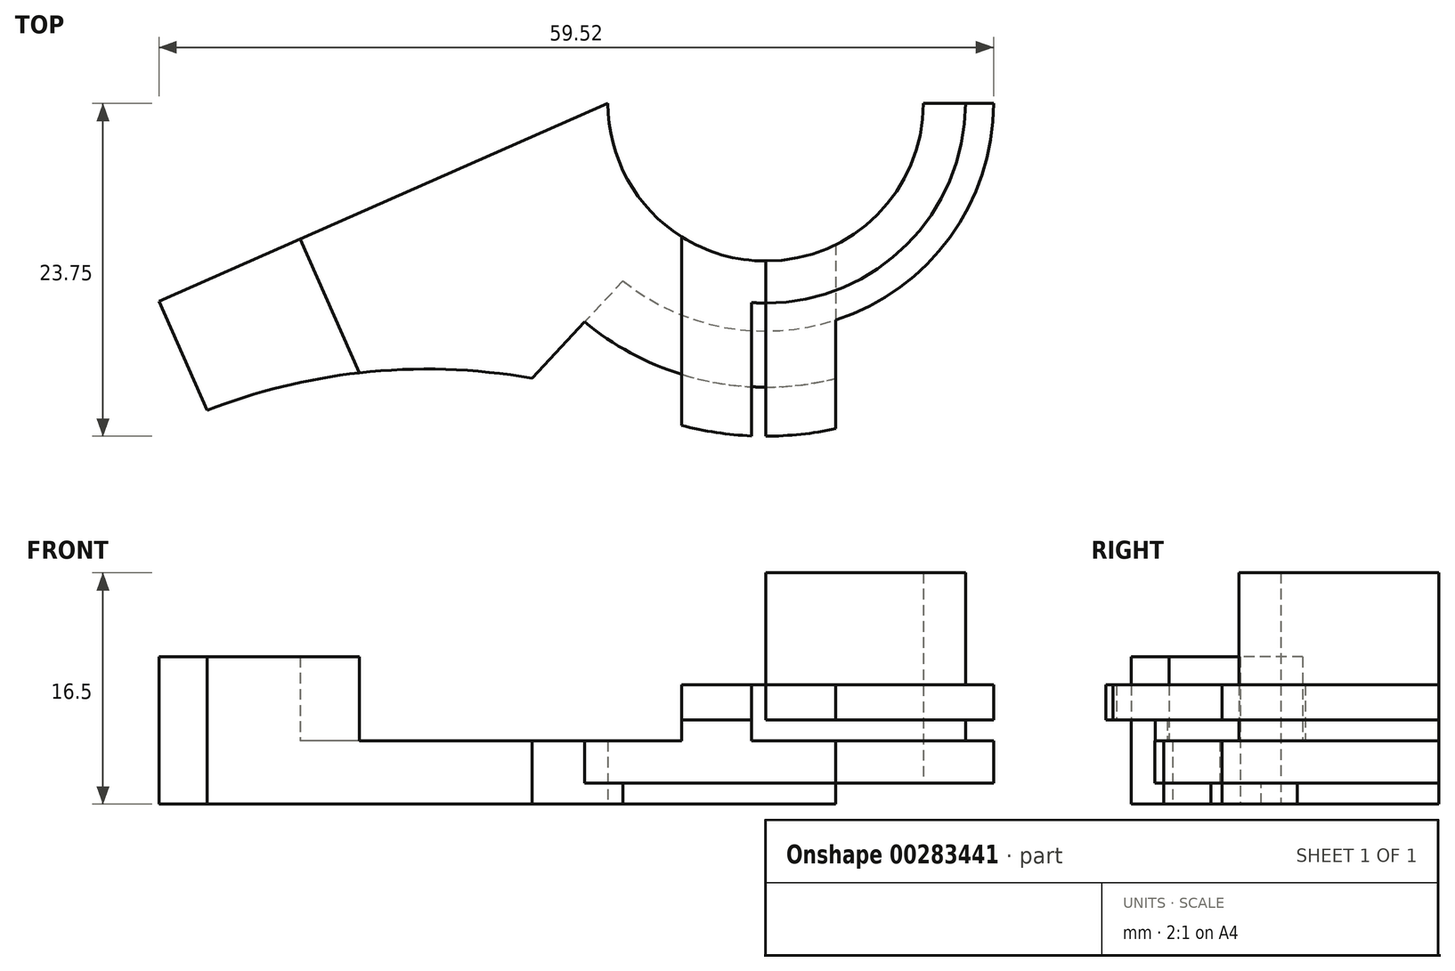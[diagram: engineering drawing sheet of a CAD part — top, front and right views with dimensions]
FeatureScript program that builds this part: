
annotation { "Feature Type Name" : "Feature", "Feature Type Description" : "" }
export const myFeature = defineFeature(function(context is Context, id is Id, definition is map)
    precondition{}
    {
        {
            var Q0;
            Q0=qCreatedBy(makeId("Top.planeOp"),FACE);
            var sketch = newSketch(context, id + "F0", { "sketchPlane" : qUnion([Q0])});
            skCircle(sketch, "E0", {"center": v(0, 0) * mm, "radius": 11.25 * mm});
            skCircle(sketch, "E1.0", {"center": v(0, 0) * mm, "radius": 14.25 * mm});
            skCircle(sketch, "E2.0", {"center": v(0, 0) * mm, "radius": 16.25 * mm});
            skCircle(sketch, "E3.0", {"center": v(0, 0) * mm, "radius": 20.25 * mm});
            skLineSegment(sketch, "E4", {"start": v(-11.25, 0) * mm, "end": v(-43.27, -14.14) * mm});
            skLineSegment(sketch, "E5", {"start": v(-43.27, -14.14) * mm, "end": v(-39.83, -21.91) * mm});
            skLineSegment(sketch, "E6", {"start": v(-12.91, -15.6) * mm, "end": v(-16.67, -19.62) * mm});
            skArc(sketch, "E7", {"start": v(-16.67, -19.62) * mm, "mid": v(-28.4, -19.17) * mm, "end": v(-39.83, -21.91) * mm});
            skLineSegment(sketch, "E8", {"start": v(-12.91, -15.6) * mm, "end": v(-10.18, -12.67) * mm});
            skLineSegment(sketch, "E9", {"start": v(-33.2, -9.7) * mm, "end": v(-29, -19.23) * mm});
            skLineSegment(sketch, "E10", {"start": v(0, 0) * mm, "end": v(0, -47.45) * mm});
            skCircle(sketch, "E11.0", {"center": v(0, 0) * mm, "radius": 23.75 * mm});
            skLineSegment(sketch, "E12.0", {"start": v(-6, 0) * mm, "end": v(-6, -47.45) * mm});
            skLineSegment(sketch, "E13.0", {"start": v(5, 0) * mm, "end": v(5, -47.45) * mm});
            skLineSegment(sketch, "E14", {"start": v(0, 0) * mm, "end": v(33.67, 0) * mm});
            skCircle(sketch, "E15.0", {"center": v(0, 0) * mm, "radius": 15.25 * mm});
            skLineSegment(sketch, "E16", {"start": v(-10.18, -12.67) * mm, "end": v(-9.5, -11.94) * mm});
            skLineSegment(sketch, "E17", {"start": v(-1, -47.36) * mm, "end": v(-1, 0) * mm});
            skSolve(sketch);
        }
        {
            var Q0;
            {var subQ0=sQuery(id+"F0.wireOp",EDGE,"E5");Q0=makeQuery(id+"F0.imprint","IMPRINT",FACE,{"disambiguationData":[TD([[makeQuery(id+"F0.imprint","IMPRINT",EDGE,{"derivedFrom":subQ0}),1.0]])]});}
            var Q1;
            {var subQ0=sQuery(id+"F0.wireOp",EDGE,"E9");Q1=makeQuery(id+"F0.imprint","IMPRINT",FACE,{"disambiguationData":[TD([[makeQuery(id+"F0.imprint","IMPRINT",EDGE,{"derivedFrom":subQ0}),1.0]])]});}
            var Q2;
            {var subQ3=sQuery(id+"F0.wireOp",EDGE,"E4");var subQ5=sQuery(id+"F0.wireOp",EDGE,"E11.0");var subQ6=makeQuery(id+"F0.imprint","INTERSECT",VERTEX,{"derivedFrom":[subQ3,subQ5]});Q2=makeQuery(id+"F0.imprint","IMPRINT",FACE,{"disambiguationData":[TD([[makeQuery(id+"F0.imprint","IMPRINT",EDGE,{"disambiguationData":[TD([[subQ6,1.0]])],"derivedFrom":subQ3}),1.0]])]});}
            var Q3;
            {var subQ0=sQuery(id+"F0.wireOp",EDGE,"E8");Q3=makeQuery(id+"F0.imprint","IMPRINT",FACE,{"disambiguationData":[TD([[makeQuery(id+"F0.imprint","IMPRINT",EDGE,{"derivedFrom":subQ0}),1.0]])]});}
            var Q4;
            {var subQ0=sQuery(id+"F0.wireOp",EDGE,"E16");Q4=makeQuery(id+"F0.imprint","IMPRINT",FACE,{"disambiguationData":[TD([[makeQuery(id+"F0.imprint","IMPRINT",EDGE,{"derivedFrom":subQ0}),1.0]])]});}
            var Q5;
            {var subQ0=sQuery(id+"F0.wireOp",EDGE,"E16");Q5=makeQuery(id+"F0.imprint","IMPRINT",FACE,{"disambiguationData":[TD([[makeQuery(id+"F0.imprint","IMPRINT",EDGE,{"derivedFrom":subQ0}),-1.0]])]});}
            var Q6;
            {var subQ0=sQuery(id+"F0.wireOp",EDGE,"E12.0");var subQ1=sQuery(id+"F0.wireOp",EDGE,"E2.0");var subQ2=makeQuery(id+"F0.imprint","INTERSECT",VERTEX,{"derivedFrom":[subQ1,subQ0]});Q6=makeQuery(id+"F0.imprint","IMPRINT",FACE,{"disambiguationData":[TD([[makeQuery(id+"F0.imprint","IMPRINT",EDGE,{"disambiguationData":[TD([[subQ2,-1.0]])],"derivedFrom":subQ1}),1.0]])]});}
            var Q7;
            {var subQ0=sQuery(id+"F0.wireOp",EDGE,"E10");var subQ1=sQuery(id+"F0.wireOp",EDGE,"E2.0");var subQ2=makeQuery(id+"F0.imprint","INTERSECT",VERTEX,{"derivedFrom":[subQ1,subQ0]});Q7=makeQuery(id+"F0.imprint","IMPRINT",FACE,{"disambiguationData":[TD([[makeQuery(id+"F0.imprint","IMPRINT",EDGE,{"disambiguationData":[TD([[subQ2,-1.0]])],"derivedFrom":subQ1}),1.0]])]});}
            var Q8;
            {var subQ0=sQuery(id+"F0.wireOp",EDGE,"E8");Q8=makeQuery(id+"F0.imprint","IMPRINT",FACE,{"disambiguationData":[TD([[makeQuery(id+"F0.imprint","IMPRINT",EDGE,{"derivedFrom":subQ0}),-1.0]])]});}
            var Q9;
            {var subQ0=sQuery(id+"F0.wireOp",EDGE,"E12.0");var subQ1=sQuery(id+"F0.wireOp",EDGE,"E2.0");var subQ2=makeQuery(id+"F0.imprint","INTERSECT",VERTEX,{"derivedFrom":[subQ1,subQ0]});Q9=makeQuery(id+"F0.imprint","IMPRINT",FACE,{"disambiguationData":[TD([[makeQuery(id+"F0.imprint","IMPRINT",EDGE,{"disambiguationData":[TD([[subQ2,-1.0]])],"derivedFrom":subQ1}),-1.0]])]});}
            var Q10;
            {var subQ0=sQuery(id+"F0.wireOp",EDGE,"E10");var subQ1=sQuery(id+"F0.wireOp",EDGE,"E2.0");var subQ2=makeQuery(id+"F0.imprint","INTERSECT",VERTEX,{"derivedFrom":[subQ1,subQ0]});Q10=makeQuery(id+"F0.imprint","IMPRINT",FACE,{"disambiguationData":[TD([[makeQuery(id+"F0.imprint","IMPRINT",EDGE,{"disambiguationData":[TD([[subQ2,-1.0]])],"derivedFrom":subQ1}),-1.0]])]});}
            var Q11;
            {var subQ0=sQuery(id+"F0.wireOp",EDGE,"E4");var subQ1=sQuery(id+"F0.wireOp",EDGE,"E0");var subQ2=makeQuery(id+"F0.imprint","INTERSECT",VERTEX,{"derivedFrom":[subQ1,subQ0]});Q11=makeQuery(id+"F0.imprint","IMPRINT",FACE,{"disambiguationData":[TD([[makeQuery(id+"F0.imprint","IMPRINT",EDGE,{"disambiguationData":[TD([[subQ2,-1.0]])],"derivedFrom":subQ1}),-1.0]])]});}
            var Q12;
            {var subQ0=sQuery(id+"F0.wireOp",EDGE,"E4");var subQ1=sQuery(id+"F0.wireOp",EDGE,"E1.0");var subQ2=makeQuery(id+"F0.imprint","INTERSECT",VERTEX,{"derivedFrom":[subQ1,subQ0]});Q12=makeQuery(id+"F0.imprint","IMPRINT",FACE,{"disambiguationData":[TD([[makeQuery(id+"F0.imprint","IMPRINT",EDGE,{"disambiguationData":[TD([[subQ2,-1.0]])],"derivedFrom":subQ1}),-1.0]])]});}
            var Q13;
            {var subQ0=sQuery(id+"F0.wireOp",EDGE,"E12.0");var subQ1=sQuery(id+"F0.wireOp",EDGE,"E0");var subQ2=makeQuery(id+"F0.imprint","INTERSECT",VERTEX,{"derivedFrom":[subQ1,subQ0]});Q13=makeQuery(id+"F0.imprint","IMPRINT",FACE,{"disambiguationData":[TD([[makeQuery(id+"F0.imprint","IMPRINT",EDGE,{"disambiguationData":[TD([[subQ2,-1.0]])],"derivedFrom":subQ1}),-1.0]])]});}
            var Q14;
            {var subQ0=sQuery(id+"F0.wireOp",EDGE,"E12.0");var subQ1=sQuery(id+"F0.wireOp",EDGE,"E1.0");var subQ2=makeQuery(id+"F0.imprint","INTERSECT",VERTEX,{"derivedFrom":[subQ1,subQ0]});Q14=makeQuery(id+"F0.imprint","IMPRINT",FACE,{"disambiguationData":[TD([[makeQuery(id+"F0.imprint","IMPRINT",EDGE,{"disambiguationData":[TD([[subQ2,-1.0]])],"derivedFrom":subQ1}),-1.0]])]});}
            var Q15;
            {var subQ0=sQuery(id+"F0.wireOp",EDGE,"E10");var subQ1=sQuery(id+"F0.wireOp",EDGE,"E0");var subQ2=makeQuery(id+"F0.imprint","INTERSECT",VERTEX,{"derivedFrom":[subQ1,subQ0]});Q15=makeQuery(id+"F0.imprint","IMPRINT",FACE,{"disambiguationData":[TD([[makeQuery(id+"F0.imprint","IMPRINT",EDGE,{"disambiguationData":[TD([[subQ2,-1.0]])],"derivedFrom":subQ1}),-1.0]])]});}
            var Q16;
            {var subQ0=sQuery(id+"F0.wireOp",EDGE,"E10");var subQ1=sQuery(id+"F0.wireOp",EDGE,"E1.0");var subQ2=makeQuery(id+"F0.imprint","INTERSECT",VERTEX,{"derivedFrom":[subQ1,subQ0]});Q16=makeQuery(id+"F0.imprint","IMPRINT",FACE,{"disambiguationData":[TD([[makeQuery(id+"F0.imprint","IMPRINT",EDGE,{"disambiguationData":[TD([[subQ2,-1.0]])],"derivedFrom":subQ1}),-1.0]])]});}
            var Q17;
            {var subQ0=sQuery(id+"F0.wireOp",EDGE,"E14");var subQ1=sQuery(id+"F0.wireOp",EDGE,"E0");var subQ2=makeQuery(id+"F0.imprint","INTERSECT",VERTEX,{"derivedFrom":[subQ1,subQ0]});Q17=makeQuery(id+"F0.imprint","IMPRINT",FACE,{"disambiguationData":[TD([[makeQuery(id+"F0.imprint","IMPRINT",EDGE,{"disambiguationData":[TD([[subQ2,1.0]])],"derivedFrom":subQ1}),-1.0]])]});}
            var Q18;
            {var subQ0=sQuery(id+"F0.wireOp",EDGE,"E14");var subQ1=sQuery(id+"F0.wireOp",EDGE,"E1.0");var subQ2=makeQuery(id+"F0.imprint","INTERSECT",VERTEX,{"derivedFrom":[subQ1,subQ0]});Q18=makeQuery(id+"F0.imprint","IMPRINT",FACE,{"disambiguationData":[TD([[makeQuery(id+"F0.imprint","IMPRINT",EDGE,{"disambiguationData":[TD([[subQ2,1.0]])],"derivedFrom":subQ1}),-1.0]])]});}
            var Q19;
            {var subQ0=sQuery(id+"F0.wireOp",EDGE,"E14");var subQ1=sQuery(id+"F0.wireOp",EDGE,"E2.0");var subQ2=makeQuery(id+"F0.imprint","INTERSECT",VERTEX,{"derivedFrom":[subQ1,subQ0]});Q19=makeQuery(id+"F0.imprint","IMPRINT",FACE,{"disambiguationData":[TD([[makeQuery(id+"F0.imprint","IMPRINT",EDGE,{"disambiguationData":[TD([[subQ2,1.0]])],"derivedFrom":subQ1}),1.0]])]});}
            var Q20;
            {var subQ0=sQuery(id+"F0.wireOp",EDGE,"E17");var subQ1=sQuery(id+"F0.wireOp",EDGE,"E2.0");var subQ2=makeQuery(id+"F0.imprint","INTERSECT",VERTEX,{"derivedFrom":[subQ1,subQ0]});Q20=makeQuery(id+"F0.imprint","IMPRINT",FACE,{"disambiguationData":[TD([[makeQuery(id+"F0.imprint","IMPRINT",EDGE,{"disambiguationData":[TD([[subQ2,-1.0]])],"derivedFrom":subQ1}),-1.0]])]});}
            var Q21;
            {var subQ0=sQuery(id+"F0.wireOp",EDGE,"E17");var subQ1=sQuery(id+"F0.wireOp",EDGE,"E2.0");var subQ2=makeQuery(id+"F0.imprint","INTERSECT",VERTEX,{"derivedFrom":[subQ1,subQ0]});Q21=makeQuery(id+"F0.imprint","IMPRINT",FACE,{"disambiguationData":[TD([[makeQuery(id+"F0.imprint","IMPRINT",EDGE,{"disambiguationData":[TD([[subQ2,-1.0]])],"derivedFrom":subQ1}),1.0]])]});}
            var Q22;
            {var subQ0=sQuery(id+"F0.wireOp",EDGE,"E17");var subQ1=sQuery(id+"F0.wireOp",EDGE,"E1.0");var subQ2=makeQuery(id+"F0.imprint","INTERSECT",VERTEX,{"derivedFrom":[subQ1,subQ0]});Q22=makeQuery(id+"F0.imprint","IMPRINT",FACE,{"disambiguationData":[TD([[makeQuery(id+"F0.imprint","IMPRINT",EDGE,{"disambiguationData":[TD([[subQ2,-1.0]])],"derivedFrom":subQ1}),-1.0]])]});}
            var Q23;
            {var subQ0=sQuery(id+"F0.wireOp",EDGE,"E17");var subQ1=sQuery(id+"F0.wireOp",EDGE,"E0");var subQ2=makeQuery(id+"F0.imprint","INTERSECT",VERTEX,{"derivedFrom":[subQ1,subQ0]});Q23=makeQuery(id+"F0.imprint","IMPRINT",FACE,{"disambiguationData":[TD([[makeQuery(id+"F0.imprint","IMPRINT",EDGE,{"disambiguationData":[TD([[subQ2,-1.0]])],"derivedFrom":subQ1}),-1.0]])]});}
            extrude(context, id + "F1", {"entities" : qUnion([Q0, Q1, Q2, Q3, Q4, Q5, Q6, Q7, Q8, Q9, Q10, Q11, Q12, Q13, Q14, Q15, Q16, Q17, Q18, Q19, Q20, Q21, Q22, Q23]), "depth" : 3 * mm});
        }
        {
            var Q0;
            {var subQ0=sQuery(id+"F0.wireOp",EDGE,"E14");var subQ1=sQuery(id+"F0.wireOp",EDGE,"E0");var subQ2=makeQuery(id+"F0.imprint","INTERSECT",VERTEX,{"derivedFrom":[subQ1,subQ0]});Q0=makeQuery(id+"F0.imprint","IMPRINT",FACE,{"disambiguationData":[TD([[makeQuery(id+"F0.imprint","IMPRINT",EDGE,{"disambiguationData":[TD([[subQ2,1.0]])],"derivedFrom":subQ1}),-1.0]])]});}
            var Q1;
            {var subQ0=sQuery(id+"F0.wireOp",EDGE,"E10");var subQ1=sQuery(id+"F0.wireOp",EDGE,"E0");var subQ2=makeQuery(id+"F0.imprint","INTERSECT",VERTEX,{"derivedFrom":[subQ1,subQ0]});Q1=makeQuery(id+"F0.imprint","IMPRINT",FACE,{"disambiguationData":[TD([[makeQuery(id+"F0.imprint","IMPRINT",EDGE,{"disambiguationData":[TD([[subQ2,-1.0]])],"derivedFrom":subQ1}),-1.0]])]});}
            var Q2;
            {var subQ0=sQuery(id+"F0.wireOp",EDGE,"E17");var subQ1=sQuery(id+"F0.wireOp",EDGE,"E0");var subQ2=makeQuery(id+"F0.imprint","INTERSECT",VERTEX,{"derivedFrom":[subQ1,subQ0]});Q2=makeQuery(id+"F0.imprint","IMPRINT",FACE,{"disambiguationData":[TD([[makeQuery(id+"F0.imprint","IMPRINT",EDGE,{"disambiguationData":[TD([[subQ2,-1.0]])],"derivedFrom":subQ1}),-1.0]])]});}
            var Q3;
            {var subQ0=sQuery(id+"F0.wireOp",EDGE,"E12.0");var subQ1=sQuery(id+"F0.wireOp",EDGE,"E0");var subQ2=makeQuery(id+"F0.imprint","INTERSECT",VERTEX,{"derivedFrom":[subQ1,subQ0]});Q3=makeQuery(id+"F0.imprint","IMPRINT",FACE,{"disambiguationData":[TD([[makeQuery(id+"F0.imprint","IMPRINT",EDGE,{"disambiguationData":[TD([[subQ2,-1.0]])],"derivedFrom":subQ1}),-1.0]])]});}
            var Q4;
            {var subQ0=sQuery(id+"F0.wireOp",EDGE,"E12.0");var subQ1=sQuery(id+"F0.wireOp",EDGE,"E1.0");var subQ2=makeQuery(id+"F0.imprint","INTERSECT",VERTEX,{"derivedFrom":[subQ1,subQ0]});Q4=makeQuery(id+"F0.imprint","IMPRINT",FACE,{"disambiguationData":[TD([[makeQuery(id+"F0.imprint","IMPRINT",EDGE,{"disambiguationData":[TD([[subQ2,-1.0]])],"derivedFrom":subQ1}),-1.0]])]});}
            var Q5;
            {var subQ0=sQuery(id+"F0.wireOp",EDGE,"E12.0");var subQ1=sQuery(id+"F0.wireOp",EDGE,"E2.0");var subQ2=makeQuery(id+"F0.imprint","INTERSECT",VERTEX,{"derivedFrom":[subQ1,subQ0]});Q5=makeQuery(id+"F0.imprint","IMPRINT",FACE,{"disambiguationData":[TD([[makeQuery(id+"F0.imprint","IMPRINT",EDGE,{"disambiguationData":[TD([[subQ2,-1.0]])],"derivedFrom":subQ1}),1.0]])]});}
            var Q6;
            {var subQ0=sQuery(id+"F0.wireOp",EDGE,"E12.0");var subQ1=sQuery(id+"F0.wireOp",EDGE,"E2.0");var subQ2=makeQuery(id+"F0.imprint","INTERSECT",VERTEX,{"derivedFrom":[subQ1,subQ0]});Q6=makeQuery(id+"F0.imprint","IMPRINT",FACE,{"disambiguationData":[TD([[makeQuery(id+"F0.imprint","IMPRINT",EDGE,{"disambiguationData":[TD([[subQ2,-1.0]])],"derivedFrom":subQ1}),-1.0]])]});}
            extrude(context, id + "F2", {"entities" : qUnion([Q0, Q1, Q2, Q3, Q4, Q5, Q6]), "operationType" : NewBodyOperationType.ADD, "depth" : 4.5 * mm});
        }
        {
            var Q0;
            {var subQ0=sQuery(id+"F0.wireOp",EDGE,"E14");var subQ1=sQuery(id+"F0.wireOp",EDGE,"E0");var subQ2=makeQuery(id+"F0.imprint","INTERSECT",VERTEX,{"derivedFrom":[subQ1,subQ0]});Q0=makeQuery(id+"F0.imprint","IMPRINT",FACE,{"disambiguationData":[TD([[makeQuery(id+"F0.imprint","IMPRINT",EDGE,{"disambiguationData":[TD([[subQ2,1.0]])],"derivedFrom":subQ1}),-1.0]])]});}
            var Q1;
            {var subQ0=sQuery(id+"F0.wireOp",EDGE,"E14");var subQ1=sQuery(id+"F0.wireOp",EDGE,"E1.0");var subQ2=makeQuery(id+"F0.imprint","INTERSECT",VERTEX,{"derivedFrom":[subQ1,subQ0]});Q1=makeQuery(id+"F0.imprint","IMPRINT",FACE,{"disambiguationData":[TD([[makeQuery(id+"F0.imprint","IMPRINT",EDGE,{"disambiguationData":[TD([[subQ2,1.0]])],"derivedFrom":subQ1}),-1.0]])]});}
            var Q2;
            {var subQ0=sQuery(id+"F0.wireOp",EDGE,"E14");var subQ1=sQuery(id+"F0.wireOp",EDGE,"E2.0");var subQ2=makeQuery(id+"F0.imprint","INTERSECT",VERTEX,{"derivedFrom":[subQ1,subQ0]});Q2=makeQuery(id+"F0.imprint","IMPRINT",FACE,{"disambiguationData":[TD([[makeQuery(id+"F0.imprint","IMPRINT",EDGE,{"disambiguationData":[TD([[subQ2,1.0]])],"derivedFrom":subQ1}),1.0]])]});}
            var Q3;
            {var subQ0=sQuery(id+"F0.wireOp",EDGE,"E10");var subQ1=sQuery(id+"F0.wireOp",EDGE,"E0");var subQ2=makeQuery(id+"F0.imprint","INTERSECT",VERTEX,{"derivedFrom":[subQ1,subQ0]});Q3=makeQuery(id+"F0.imprint","IMPRINT",FACE,{"disambiguationData":[TD([[makeQuery(id+"F0.imprint","IMPRINT",EDGE,{"disambiguationData":[TD([[subQ2,-1.0]])],"derivedFrom":subQ1}),-1.0]])]});}
            var Q4;
            {var subQ0=sQuery(id+"F0.wireOp",EDGE,"E10");var subQ1=sQuery(id+"F0.wireOp",EDGE,"E1.0");var subQ2=makeQuery(id+"F0.imprint","INTERSECT",VERTEX,{"derivedFrom":[subQ1,subQ0]});Q4=makeQuery(id+"F0.imprint","IMPRINT",FACE,{"disambiguationData":[TD([[makeQuery(id+"F0.imprint","IMPRINT",EDGE,{"disambiguationData":[TD([[subQ2,-1.0]])],"derivedFrom":subQ1}),-1.0]])]});}
            var Q5;
            {var subQ0=sQuery(id+"F0.wireOp",EDGE,"E10");var subQ1=sQuery(id+"F0.wireOp",EDGE,"E2.0");var subQ2=makeQuery(id+"F0.imprint","INTERSECT",VERTEX,{"derivedFrom":[subQ1,subQ0]});Q5=makeQuery(id+"F0.imprint","IMPRINT",FACE,{"disambiguationData":[TD([[makeQuery(id+"F0.imprint","IMPRINT",EDGE,{"disambiguationData":[TD([[subQ2,-1.0]])],"derivedFrom":subQ1}),1.0]])]});}
            var Q6;
            {var subQ0=sQuery(id+"F0.wireOp",EDGE,"E10");var subQ1=sQuery(id+"F0.wireOp",EDGE,"E2.0");var subQ2=makeQuery(id+"F0.imprint","INTERSECT",VERTEX,{"derivedFrom":[subQ1,subQ0]});Q6=makeQuery(id+"F0.imprint","IMPRINT",FACE,{"disambiguationData":[TD([[makeQuery(id+"F0.imprint","IMPRINT",EDGE,{"disambiguationData":[TD([[subQ2,-1.0]])],"derivedFrom":subQ1}),-1.0]])]});}
            var Q7;
            {var subQ0=sQuery(id+"F0.wireOp",EDGE,"E17");var subQ1=sQuery(id+"F0.wireOp",EDGE,"E0");var subQ2=makeQuery(id+"F0.imprint","INTERSECT",VERTEX,{"derivedFrom":[subQ1,subQ0]});Q7=makeQuery(id+"F0.imprint","IMPRINT",FACE,{"disambiguationData":[TD([[makeQuery(id+"F0.imprint","IMPRINT",EDGE,{"disambiguationData":[TD([[subQ2,-1.0]])],"derivedFrom":subQ1}),-1.0]])]});}
            var Q8;
            {var subQ0=sQuery(id+"F0.wireOp",EDGE,"E12.0");var subQ1=sQuery(id+"F0.wireOp",EDGE,"E0");var subQ2=makeQuery(id+"F0.imprint","INTERSECT",VERTEX,{"derivedFrom":[subQ1,subQ0]});Q8=makeQuery(id+"F0.imprint","IMPRINT",FACE,{"disambiguationData":[TD([[makeQuery(id+"F0.imprint","IMPRINT",EDGE,{"disambiguationData":[TD([[subQ2,-1.0]])],"derivedFrom":subQ1}),-1.0]])]});}
            var Q9;
            {var subQ0=sQuery(id+"F0.wireOp",EDGE,"E12.0");var subQ1=sQuery(id+"F0.wireOp",EDGE,"E1.0");var subQ2=makeQuery(id+"F0.imprint","INTERSECT",VERTEX,{"derivedFrom":[subQ1,subQ0]});Q9=makeQuery(id+"F0.imprint","IMPRINT",FACE,{"disambiguationData":[TD([[makeQuery(id+"F0.imprint","IMPRINT",EDGE,{"disambiguationData":[TD([[subQ2,-1.0]])],"derivedFrom":subQ1}),-1.0]])]});}
            var Q10;
            {var subQ0=sQuery(id+"F0.wireOp",EDGE,"E12.0");var subQ1=sQuery(id+"F0.wireOp",EDGE,"E2.0");var subQ2=makeQuery(id+"F0.imprint","INTERSECT",VERTEX,{"derivedFrom":[subQ1,subQ0]});Q10=makeQuery(id+"F0.imprint","IMPRINT",FACE,{"disambiguationData":[TD([[makeQuery(id+"F0.imprint","IMPRINT",EDGE,{"disambiguationData":[TD([[subQ2,-1.0]])],"derivedFrom":subQ1}),1.0]])]});}
            var Q11;
            {var subQ0=sQuery(id+"F0.wireOp",EDGE,"E12.0");var subQ1=sQuery(id+"F0.wireOp",EDGE,"E2.0");var subQ2=makeQuery(id+"F0.imprint","INTERSECT",VERTEX,{"derivedFrom":[subQ1,subQ0]});Q11=makeQuery(id+"F0.imprint","IMPRINT",FACE,{"disambiguationData":[TD([[makeQuery(id+"F0.imprint","IMPRINT",EDGE,{"disambiguationData":[TD([[subQ2,-1.0]])],"derivedFrom":subQ1}),-1.0]])]});}
            var Q12;
            {var subQ0=sQuery(id+"F0.wireOp",EDGE,"E10");var subQ1=sQuery(id+"F0.wireOp",EDGE,"E3.0");var subQ2=makeQuery(id+"F0.imprint","INTERSECT",VERTEX,{"derivedFrom":[subQ1,subQ0]});Q12=makeQuery(id+"F0.imprint","IMPRINT",FACE,{"disambiguationData":[TD([[makeQuery(id+"F0.imprint","IMPRINT",EDGE,{"disambiguationData":[TD([[subQ2,-1.0]])],"derivedFrom":subQ1}),-1.0]])]});}
            var Q13;
            {var subQ0=sQuery(id+"F0.wireOp",EDGE,"E12.0");var subQ1=sQuery(id+"F0.wireOp",EDGE,"E3.0");var subQ2=makeQuery(id+"F0.imprint","INTERSECT",VERTEX,{"derivedFrom":[subQ1,subQ0]});Q13=makeQuery(id+"F0.imprint","IMPRINT",FACE,{"disambiguationData":[TD([[makeQuery(id+"F0.imprint","IMPRINT",EDGE,{"disambiguationData":[TD([[subQ2,-1.0]])],"derivedFrom":subQ1}),-1.0]])]});}
            extrude(context, id + "F3", {"entities" : qUnion([Q0, Q1, Q2, Q3, Q4, Q5, Q6, Q7, Q8, Q9, Q10, Q11, Q12, Q13]), "operationType" : NewBodyOperationType.ADD, "depth" : 7 * mm, "hasSecondDirection" : true, "secondDirectionOppositeDirection" : false, "secondDirectionDepth" : 4.5 * mm});
        }
        {
            var Q0;
            {var subQ0=sQuery(id+"F0.wireOp",EDGE,"E14");var subQ1=sQuery(id+"F0.wireOp",EDGE,"E0");var subQ2=makeQuery(id+"F0.imprint","INTERSECT",VERTEX,{"derivedFrom":[subQ1,subQ0]});Q0=makeQuery(id+"F0.imprint","IMPRINT",FACE,{"disambiguationData":[TD([[makeQuery(id+"F0.imprint","IMPRINT",EDGE,{"disambiguationData":[TD([[subQ2,1.0]])],"derivedFrom":subQ1}),-1.0]])]});}
            var Q1;
            {var subQ0=sQuery(id+"F0.wireOp",EDGE,"E10");var subQ1=sQuery(id+"F0.wireOp",EDGE,"E0");var subQ2=makeQuery(id+"F0.imprint","INTERSECT",VERTEX,{"derivedFrom":[subQ1,subQ0]});Q1=makeQuery(id+"F0.imprint","IMPRINT",FACE,{"disambiguationData":[TD([[makeQuery(id+"F0.imprint","IMPRINT",EDGE,{"disambiguationData":[TD([[subQ2,-1.0]])],"derivedFrom":subQ1}),-1.0]])]});}
            extrude(context, id + "F4", {"entities" : qUnion([Q0, Q1]), "operationType" : NewBodyOperationType.ADD, "depth" : 15 * mm});
        }
        {
            var Q0;
            {var subQ0=sQuery(id+"F0.wireOp",EDGE,"E5");Q0=makeQuery(id+"F0.imprint","IMPRINT",FACE,{"disambiguationData":[TD([[makeQuery(id+"F0.imprint","IMPRINT",EDGE,{"derivedFrom":subQ0}),1.0]])]});}
            extrude(context, id + "F5", {"entities" : qUnion([Q0]), "operationType" : NewBodyOperationType.ADD, "depth" : 9 * mm});
        }
        {
            var Q0;
            {var subQ0=sQuery(id+"F0.wireOp",EDGE,"E5");Q0=makeQuery(id+"F0.imprint","IMPRINT",FACE,{"disambiguationData":[TD([[makeQuery(id+"F0.imprint","IMPRINT",EDGE,{"derivedFrom":subQ0}),1.0]])]});}
            var Q1;
            {var subQ0=sQuery(id+"F0.wireOp",EDGE,"E9");Q1=makeQuery(id+"F0.imprint","IMPRINT",FACE,{"disambiguationData":[TD([[makeQuery(id+"F0.imprint","IMPRINT",EDGE,{"derivedFrom":subQ0}),1.0]])]});}
            var Q2;
            {var subQ3=sQuery(id+"F0.wireOp",EDGE,"E4");var subQ5=sQuery(id+"F0.wireOp",EDGE,"E11.0");var subQ7=makeQuery(id+"F0.imprint","INTERSECT",VERTEX,{"derivedFrom":[subQ3,subQ5]});Q2=makeQuery(id+"F0.imprint","IMPRINT",FACE,{"disambiguationData":[TD([[makeQuery(id+"F0.imprint","IMPRINT",EDGE,{"disambiguationData":[TD([[subQ7,1.0]])],"derivedFrom":subQ3}),1.0]])]});}
            var Q3;
            {var subQ0=sQuery(id+"F0.wireOp",EDGE,"E8");Q3=makeQuery(id+"F0.imprint","IMPRINT",FACE,{"disambiguationData":[TD([[makeQuery(id+"F0.imprint","IMPRINT",EDGE,{"derivedFrom":subQ0}),1.0]])]});}
            var Q4;
            {var subQ0=sQuery(id+"F0.wireOp",EDGE,"E16");Q4=makeQuery(id+"F0.imprint","IMPRINT",FACE,{"disambiguationData":[TD([[makeQuery(id+"F0.imprint","IMPRINT",EDGE,{"derivedFrom":subQ0}),1.0]])]});}
            var Q5;
            {var subQ1=sQuery(id+"F0.wireOp",EDGE,"E1.0");var subQ6=sQuery(id+"F0.wireOp",EDGE,"E4");var subQ8=makeQuery(id+"F0.imprint","INTERSECT",VERTEX,{"derivedFrom":[subQ1,subQ6]});Q5=makeQuery(id+"F0.imprint","IMPRINT",FACE,{"disambiguationData":[TD([[makeQuery(id+"F0.imprint","IMPRINT",EDGE,{"disambiguationData":[TD([[subQ8,-1.0]])],"derivedFrom":subQ1}),-1.0]])]});}
            var Q6;
            {var subQ0=sQuery(id+"F0.wireOp",EDGE,"E4");var subQ1=sQuery(id+"F0.wireOp",EDGE,"E0");var subQ2=makeQuery(id+"F0.imprint","INTERSECT",VERTEX,{"derivedFrom":[subQ1,subQ0]});Q6=makeQuery(id+"F0.imprint","IMPRINT",FACE,{"disambiguationData":[TD([[makeQuery(id+"F0.imprint","IMPRINT",EDGE,{"disambiguationData":[TD([[subQ2,-1.0]])],"derivedFrom":subQ1}),-1.0]])]});}
            var Q7;
            {var subQ0=sQuery(id+"F0.wireOp",EDGE,"E16");Q7=makeQuery(id+"F0.imprint","IMPRINT",FACE,{"disambiguationData":[TD([[makeQuery(id+"F0.imprint","IMPRINT",EDGE,{"derivedFrom":subQ0}),-1.0]])]});}
            var Q8;
            {var subQ0=sQuery(id+"F0.wireOp",EDGE,"E12.0");var subQ1=sQuery(id+"F0.wireOp",EDGE,"E0");var subQ2=makeQuery(id+"F0.imprint","INTERSECT",VERTEX,{"derivedFrom":[subQ1,subQ0]});Q8=makeQuery(id+"F0.imprint","IMPRINT",FACE,{"disambiguationData":[TD([[makeQuery(id+"F0.imprint","IMPRINT",EDGE,{"disambiguationData":[TD([[subQ2,-1.0]])],"derivedFrom":subQ1}),-1.0]])]});}
            var Q9;
            {var subQ0=sQuery(id+"F0.wireOp",EDGE,"E12.0");var subQ1=sQuery(id+"F0.wireOp",EDGE,"E1.0");var subQ2=makeQuery(id+"F0.imprint","INTERSECT",VERTEX,{"derivedFrom":[subQ1,subQ0]});Q9=makeQuery(id+"F0.imprint","IMPRINT",FACE,{"disambiguationData":[TD([[makeQuery(id+"F0.imprint","IMPRINT",EDGE,{"disambiguationData":[TD([[subQ2,-1.0]])],"derivedFrom":subQ1}),-1.0]])]});}
            var Q10;
            {var subQ0=sQuery(id+"F0.wireOp",EDGE,"E12.0");var subQ1=sQuery(id+"F0.wireOp",EDGE,"E2.0");var subQ2=makeQuery(id+"F0.imprint","INTERSECT",VERTEX,{"derivedFrom":[subQ1,subQ0]});Q10=makeQuery(id+"F0.imprint","IMPRINT",FACE,{"disambiguationData":[TD([[makeQuery(id+"F0.imprint","IMPRINT",EDGE,{"disambiguationData":[TD([[subQ2,-1.0]])],"derivedFrom":subQ1}),1.0]])]});}
            var Q11;
            {var subQ0=sQuery(id+"F0.wireOp",EDGE,"E10");var subQ1=sQuery(id+"F0.wireOp",EDGE,"E0");var subQ2=makeQuery(id+"F0.imprint","INTERSECT",VERTEX,{"derivedFrom":[subQ1,subQ0]});Q11=makeQuery(id+"F0.imprint","IMPRINT",FACE,{"disambiguationData":[TD([[makeQuery(id+"F0.imprint","IMPRINT",EDGE,{"disambiguationData":[TD([[subQ2,-1.0]])],"derivedFrom":subQ1}),-1.0]])]});}
            var Q12;
            {var subQ0=sQuery(id+"F0.wireOp",EDGE,"E10");var subQ1=sQuery(id+"F0.wireOp",EDGE,"E1.0");var subQ2=makeQuery(id+"F0.imprint","INTERSECT",VERTEX,{"derivedFrom":[subQ1,subQ0]});Q12=makeQuery(id+"F0.imprint","IMPRINT",FACE,{"disambiguationData":[TD([[makeQuery(id+"F0.imprint","IMPRINT",EDGE,{"disambiguationData":[TD([[subQ2,-1.0]])],"derivedFrom":subQ1}),-1.0]])]});}
            var Q13;
            {var subQ0=sQuery(id+"F0.wireOp",EDGE,"E10");var subQ1=sQuery(id+"F0.wireOp",EDGE,"E2.0");var subQ2=makeQuery(id+"F0.imprint","INTERSECT",VERTEX,{"derivedFrom":[subQ1,subQ0]});Q13=makeQuery(id+"F0.imprint","IMPRINT",FACE,{"disambiguationData":[TD([[makeQuery(id+"F0.imprint","IMPRINT",EDGE,{"disambiguationData":[TD([[subQ2,-1.0]])],"derivedFrom":subQ1}),1.0]])]});}
            var Q14;
            {var subQ0=sQuery(id+"F0.wireOp",EDGE,"E17");var subQ1=sQuery(id+"F0.wireOp",EDGE,"E2.0");var subQ2=makeQuery(id+"F0.imprint","INTERSECT",VERTEX,{"derivedFrom":[subQ1,subQ0]});Q14=makeQuery(id+"F0.imprint","IMPRINT",FACE,{"disambiguationData":[TD([[makeQuery(id+"F0.imprint","IMPRINT",EDGE,{"disambiguationData":[TD([[subQ2,-1.0]])],"derivedFrom":subQ1}),1.0]])]});}
            var Q15;
            {var subQ0=sQuery(id+"F0.wireOp",EDGE,"E17");var subQ1=sQuery(id+"F0.wireOp",EDGE,"E1.0");var subQ2=makeQuery(id+"F0.imprint","INTERSECT",VERTEX,{"derivedFrom":[subQ1,subQ0]});Q15=makeQuery(id+"F0.imprint","IMPRINT",FACE,{"disambiguationData":[TD([[makeQuery(id+"F0.imprint","IMPRINT",EDGE,{"disambiguationData":[TD([[subQ2,-1.0]])],"derivedFrom":subQ1}),-1.0]])]});}
            var Q16;
            {var subQ0=sQuery(id+"F0.wireOp",EDGE,"E17");var subQ1=sQuery(id+"F0.wireOp",EDGE,"E0");var subQ2=makeQuery(id+"F0.imprint","INTERSECT",VERTEX,{"derivedFrom":[subQ1,subQ0]});Q16=makeQuery(id+"F0.imprint","IMPRINT",FACE,{"disambiguationData":[TD([[makeQuery(id+"F0.imprint","IMPRINT",EDGE,{"disambiguationData":[TD([[subQ2,-1.0]])],"derivedFrom":subQ1}),-1.0]])]});}
            extrude(context, id + "F6", {"entities" : qUnion([Q0, Q1, Q2, Q3, Q4, Q5, Q6, Q7, Q8, Q9, Q10, Q11, Q12, Q13, Q14, Q15, Q16]), "operationType" : NewBodyOperationType.ADD, "oppositeDirection" : true, "depth" : 1.5 * mm});
        }
    });
